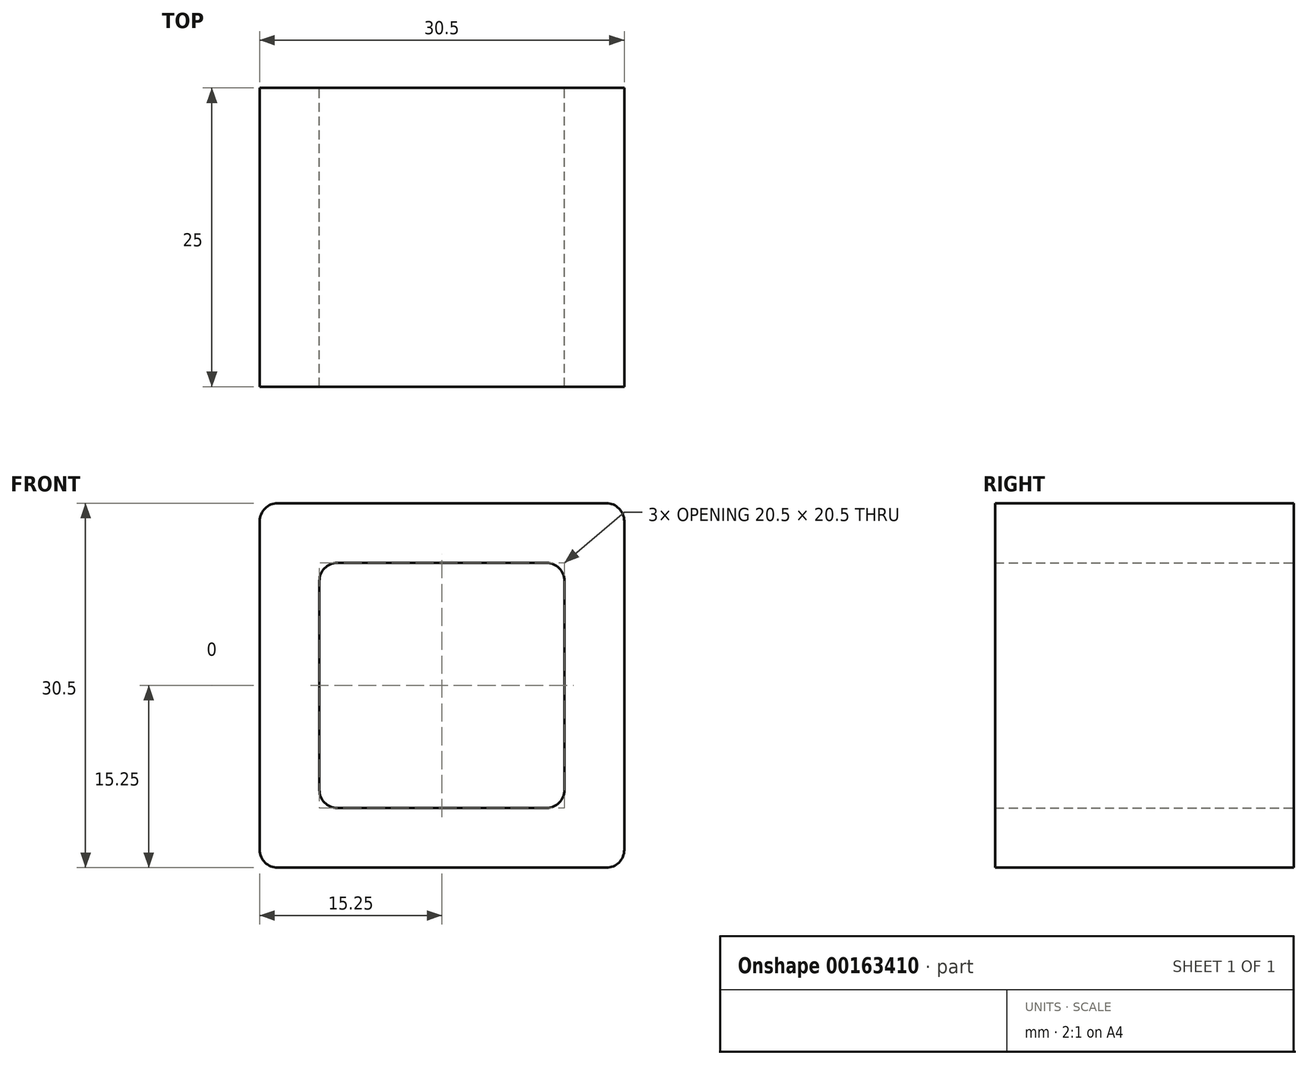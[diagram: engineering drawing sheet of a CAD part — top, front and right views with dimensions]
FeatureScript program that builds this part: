
annotation { "Feature Type Name" : "Feature", "Feature Type Description" : "" }
export const myFeature = defineFeature(function(context is Context, id is Id, definition is map)
    precondition{}
    {
        {
            var Q0;
            Q0=qCreatedBy(makeId("Front.planeOp"),FACE);
            var sketch = newSketch(context, id + "F0", { "sketchPlane" : qUnion([Q0])});
            skLineSegment(sketch, "E0.bottom", {"start": v(-9, 15) * mm, "end": v(8.5, 15) * mm});
            skLineSegment(sketch, "E0.top", {"start": v(-9, -5.5) * mm, "end": v(8.5, -5.5) * mm});
            skLineSegment(sketch, "E0.left", {"start": v(-10.5, 13.5) * mm, "end": v(-10.5, -4) * mm});
            skLineSegment(sketch, "E0.right", {"start": v(10, 13.5) * mm, "end": v(10, -4) * mm});
            skLineSegment(sketch, "E1.bottom", {"start": v(-14, 20) * mm, "end": v(13.5, 20) * mm});
            skLineSegment(sketch, "E1.top", {"start": v(-14, -10.5) * mm, "end": v(13.5, -10.5) * mm});
            skLineSegment(sketch, "E1.left", {"start": v(-15.5, 18.5) * mm, "end": v(-15.5, -9) * mm});
            skLineSegment(sketch, "E1.right", {"start": v(15, 18.5) * mm, "end": v(15, -9) * mm});
            skPoint(sketch, "E2.visualSharp", {"position": v(-10.5, 15) * mm});
            skArc(sketch, "E2.filletArc", {"start": v(-9, 15) * mm, "mid": v(-10.06, 14.56) * mm, "end": v(-10.5, 13.5) * mm});
            skPoint(sketch, "E3.visualSharp", {"position": v(10, 15) * mm});
            skArc(sketch, "E3.filletArc", {"start": v(10, 13.5) * mm, "mid": v(9.56, 14.56) * mm, "end": v(8.5, 15) * mm});
            skPoint(sketch, "E4.visualSharp", {"position": v(-10.5, -5.5) * mm});
            skArc(sketch, "E4.filletArc", {"start": v(-10.5, -4) * mm, "mid": v(-10.06, -5.06) * mm, "end": v(-9, -5.5) * mm});
            skPoint(sketch, "E5.visualSharp", {"position": v(10, -5.5) * mm});
            skArc(sketch, "E5.filletArc", {"start": v(8.5, -5.5) * mm, "mid": v(9.56, -5.06) * mm, "end": v(10, -4) * mm});
            skPoint(sketch, "E6.visualSharp", {"position": v(-15.5, 20) * mm});
            skArc(sketch, "E6.filletArc", {"start": v(-14, 20) * mm, "mid": v(-15.06, 19.56) * mm, "end": v(-15.5, 18.5) * mm});
            skPoint(sketch, "E7.visualSharp", {"position": v(15, 20) * mm});
            skArc(sketch, "E7.filletArc", {"start": v(15, 18.5) * mm, "mid": v(14.56, 19.56) * mm, "end": v(13.5, 20) * mm});
            skPoint(sketch, "E8.visualSharp", {"position": v(15, -10.5) * mm});
            skArc(sketch, "E8.filletArc", {"start": v(13.5, -10.5) * mm, "mid": v(14.56, -10.06) * mm, "end": v(15, -9) * mm});
            skPoint(sketch, "E9.visualSharp", {"position": v(-15.5, -10.5) * mm});
            skArc(sketch, "E9.filletArc", {"start": v(-15.5, -9) * mm, "mid": v(-15.06, -10.06) * mm, "end": v(-14, -10.5) * mm});
            skSolve(sketch);
        }
        {
            var Q0;
            Q0=makeQuery(id+"F0.imprint","IMPRINT",FACE,{"disambiguationData":[TD([[makeQuery(id+"F0.imprint","IMPRINT",EDGE,{"derivedFrom":sQuery(id+"F0.wireOp",EDGE,"E0.bottom")}),1.0]])]});
            extrude(context, id + "F1", {"entities" : qUnion([Q0]), "depth" : 25 * mm});
        }
    });
